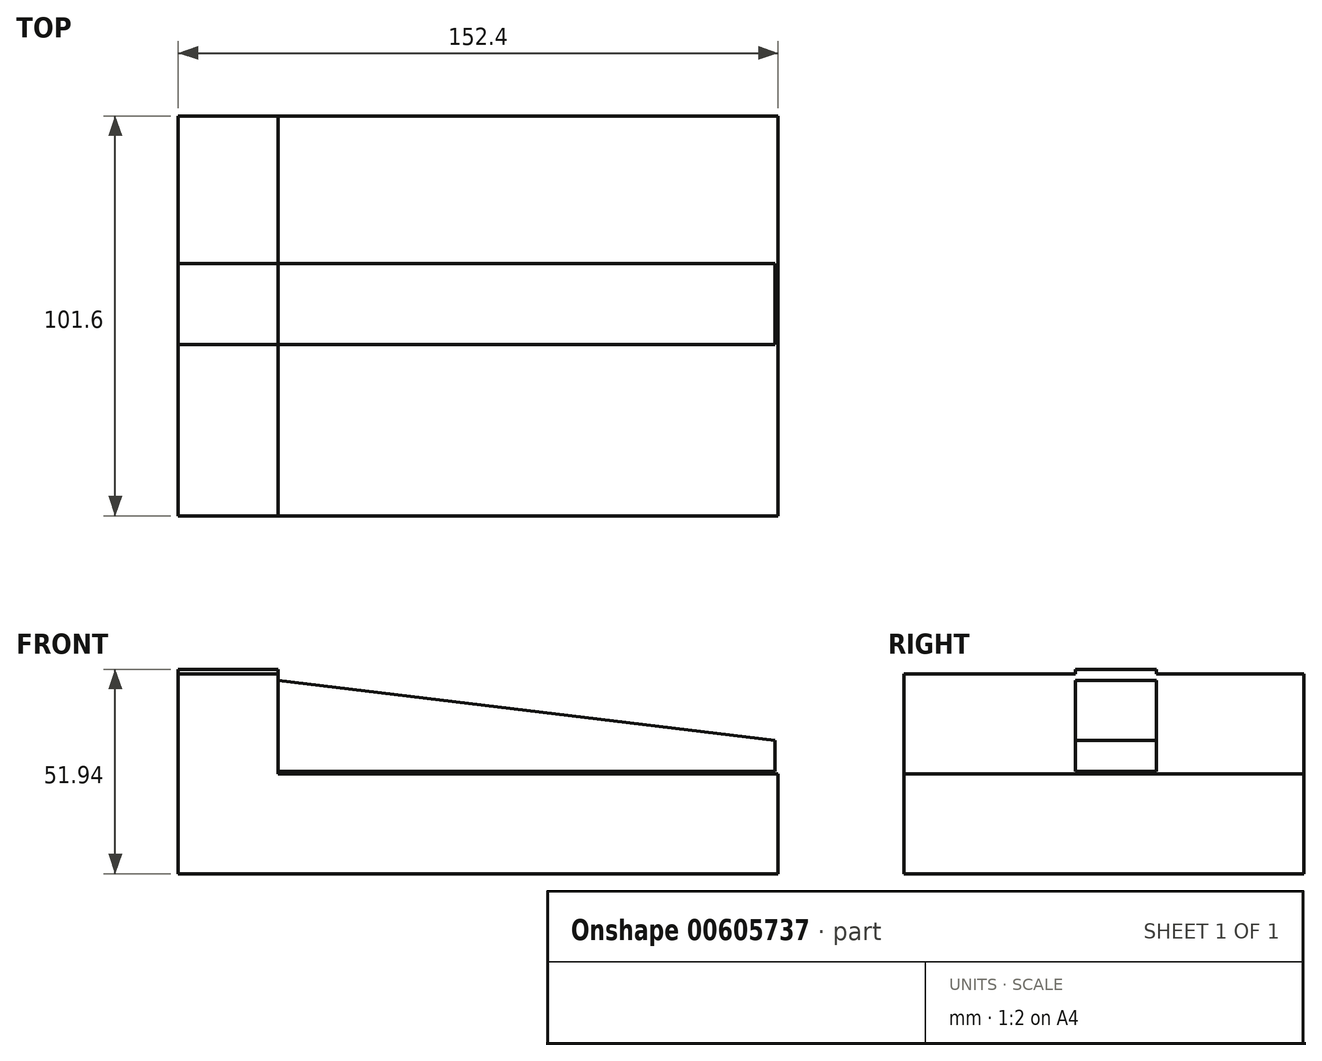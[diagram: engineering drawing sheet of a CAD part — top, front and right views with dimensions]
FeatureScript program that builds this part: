
annotation { "Feature Type Name" : "Feature", "Feature Type Description" : "" }
export const myFeature = defineFeature(function(context is Context, id is Id, definition is map)
    precondition{}
    {
        {
            var Q0;
            Q0=qCreatedBy(makeId("Front.planeOp"),FACE);
            var sketch = newSketch(context, id + "F0", { "sketchPlane" : qUnion([Q0])});
            skLineSegment(sketch, "E0", {"start": v(0, 0) * mm, "end": v(0, 50.8) * mm});
            skLineSegment(sketch, "E1", {"start": v(0, 0) * mm, "end": v(152.4, 0) * mm});
            skLineSegment(sketch, "E2", {"start": v(152.4, 0) * mm, "end": v(152.4, 25.4) * mm});
            skLineSegment(sketch, "E3", {"start": v(152.4, 25.4) * mm, "end": v(25.4, 25.4) * mm});
            skLineSegment(sketch, "E4", {"start": v(25.4, 25.4) * mm, "end": v(25.4, 50.8) * mm});
            skLineSegment(sketch, "E5", {"start": v(0, 50.8) * mm, "end": v(25.4, 50.8) * mm});
            skLineSegment(sketch, "E6", {"start": v(25.4, 50.8) * mm, "end": v(152.4, 25.4) * mm});
            skSolve(sketch);
        }
        {
            var Q0;
            Q0=makeQuery(id+"F0.imprint","IMPRINT",FACE,{"disambiguationData":[TD([[makeQuery(id+"F0.imprint","IMPRINT",EDGE,{"derivedFrom":sQuery(id+"F0.wireOp",EDGE,"E0")}),-1.0]])]});
            extrude(context, id + "F1", {"entities" : qUnion([Q0]), "depth" : 101.6 * mm, "offsetDistance" : 25.4 * mm});
        }
        {
            var Q0;
            Q0=qCreatedBy(makeId("Right.planeOp"),FACE);
            var sketch = newSketch(context, id + "F2", { "sketchPlane" : qUnion([Q0])});
            skLineSegment(sketch, "E7.bottom", {"start": v(-58.04, 51.44) * mm, "end": v(-37.46, 51.44) * mm});
            skLineSegment(sketch, "E7.top", {"start": v(-58.04, 26.04) * mm, "end": v(-37.46, 26.04) * mm});
            skLineSegment(sketch, "E7.left", {"start": v(-58.04, 51.44) * mm, "end": v(-58.04, 26.04) * mm});
            skLineSegment(sketch, "E7.right", {"start": v(-37.46, 51.44) * mm, "end": v(-37.46, 26.04) * mm});
            skSolve(sketch);
        }
        {
            var Q0;
            Q0=makeQuery(id+"F2.imprint","IMPRINT",FACE,{"disambiguationData":[TD([[makeQuery(id+"F2.imprint","IMPRINT",EDGE,{"derivedFrom":sQuery(id+"F2.wireOp",EDGE,"E7.bottom")}),-1.0]])]});
            extrude(context, id + "F3", {"entities" : qUnion([Q0]), "operationType" : NewBodyOperationType.ADD, "depth" : 151.64 * mm, "offsetDistance" : 25.4 * mm});
        }
        {
            var Q0;
            Q0=makeQuery(id+"F3.opExtrude","SWEPT_FACE",FACE,{"disambiguationData":[OSD([sQuery(id+"F2.wireOp",EDGE,"E7.bottom")])]});
            extrude(context, id + "F4", {"entities" : qUnion([Q0]), "operationType" : NewBodyOperationType.REMOVE, "oppositeDirection" : true, "depth" : 2.3 * mm, "offsetDistance" : 25.4 * mm});
        }
        {
            var Q0;
            Q0=makeQuery(id+"F3.opExtrude","SWEPT_FACE",FACE,{"disambiguationData":[OSD([sQuery(id+"F2.wireOp",EDGE,"E7.left")])]});
            var sketch = newSketch(context, id + "F5", { "sketchPlane" : qUnion([Q0])});
            skLineSegment(sketch, "E8", {"start": v(25.4, 49.15) * mm, "end": v(151.64, 33.88) * mm});
            skSolve(sketch);
        }
        {
            var Q0;
            {var subQ0=sQuery(id+"F5.wireOp",EDGE,"E8");Q0=makeQuery(id+"F5.imprint","IMPRINT",FACE,{"disambiguationData":[TD([[makeQuery(id+"F5.imprint","IMPRINT",EDGE,{"derivedFrom":subQ0}),1.0]])]});}
            extrude(context, id + "F6", {"entities" : qUnion([Q0]), "operationType" : NewBodyOperationType.REMOVE, "oppositeDirection" : true, "depth" : 32.5 * mm, "offsetDistance" : 25.4 * mm});
        }
        {
            var Q0;
            Q0=makeQuery(id+"F4.boolean.opBoolean","COPY",FACE,{"derivedFrom":makeQuery(id+"F4.opExtrude","CAP_FACE",FACE,{"disambiguationData":[OSD([sQuery(id+"F2.wireOp",EDGE,"E7.bottom")])],"isStart":false})});
            extrude(context, id + "F7", {"entities" : qUnion([Q0]), "operationType" : NewBodyOperationType.ADD, "depth" : 2.8 * mm, "offsetDistance" : 25.4 * mm});
        }
    });
